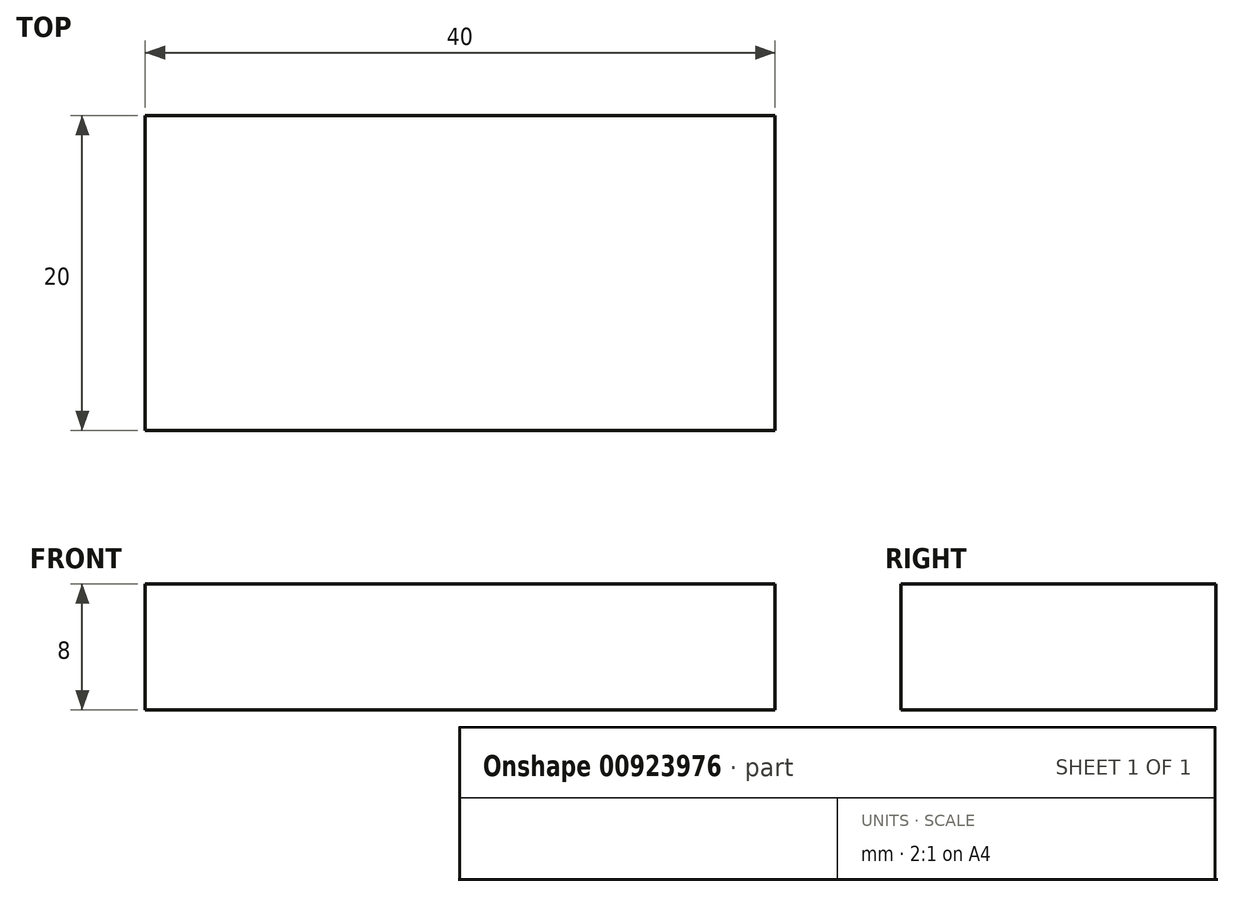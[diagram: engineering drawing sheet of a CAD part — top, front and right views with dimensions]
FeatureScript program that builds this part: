
annotation { "Feature Type Name" : "Feature", "Feature Type Description" : "" }
export const myFeature = defineFeature(function(context is Context, id is Id, definition is map)
    precondition{}
    {
        {
            var Q0;
            Q0=qCreatedBy(makeId("Top.planeOp"),FACE);
            var sketch = newSketch(context, id + "F0", { "sketchPlane" : qUnion([Q0])});
            skLineSegment(sketch, "E0.bottom", {"start": v(20, -10) * mm, "end": v(-20, -10) * mm});
            skLineSegment(sketch, "E0.top", {"start": v(20, 10) * mm, "end": v(-20, 10) * mm});
            skLineSegment(sketch, "E0.left", {"start": v(20, -10) * mm, "end": v(20, 10) * mm});
            skLineSegment(sketch, "E0.right", {"start": v(-20, -10) * mm, "end": v(-20, 10) * mm});
            skPoint(sketch, "E0.middle", {"position": v(0, 0) * mm});
            skSolve(sketch);
        }
        {
            var Q0;
            Q0 = qSketchRegion(id + "F0", true);
            extrude(context, id + "F1", {"entities" : qUnion([Q0]), "depth" : 8 * mm, "offsetDistance" : 25 * mm});
        }
    });
